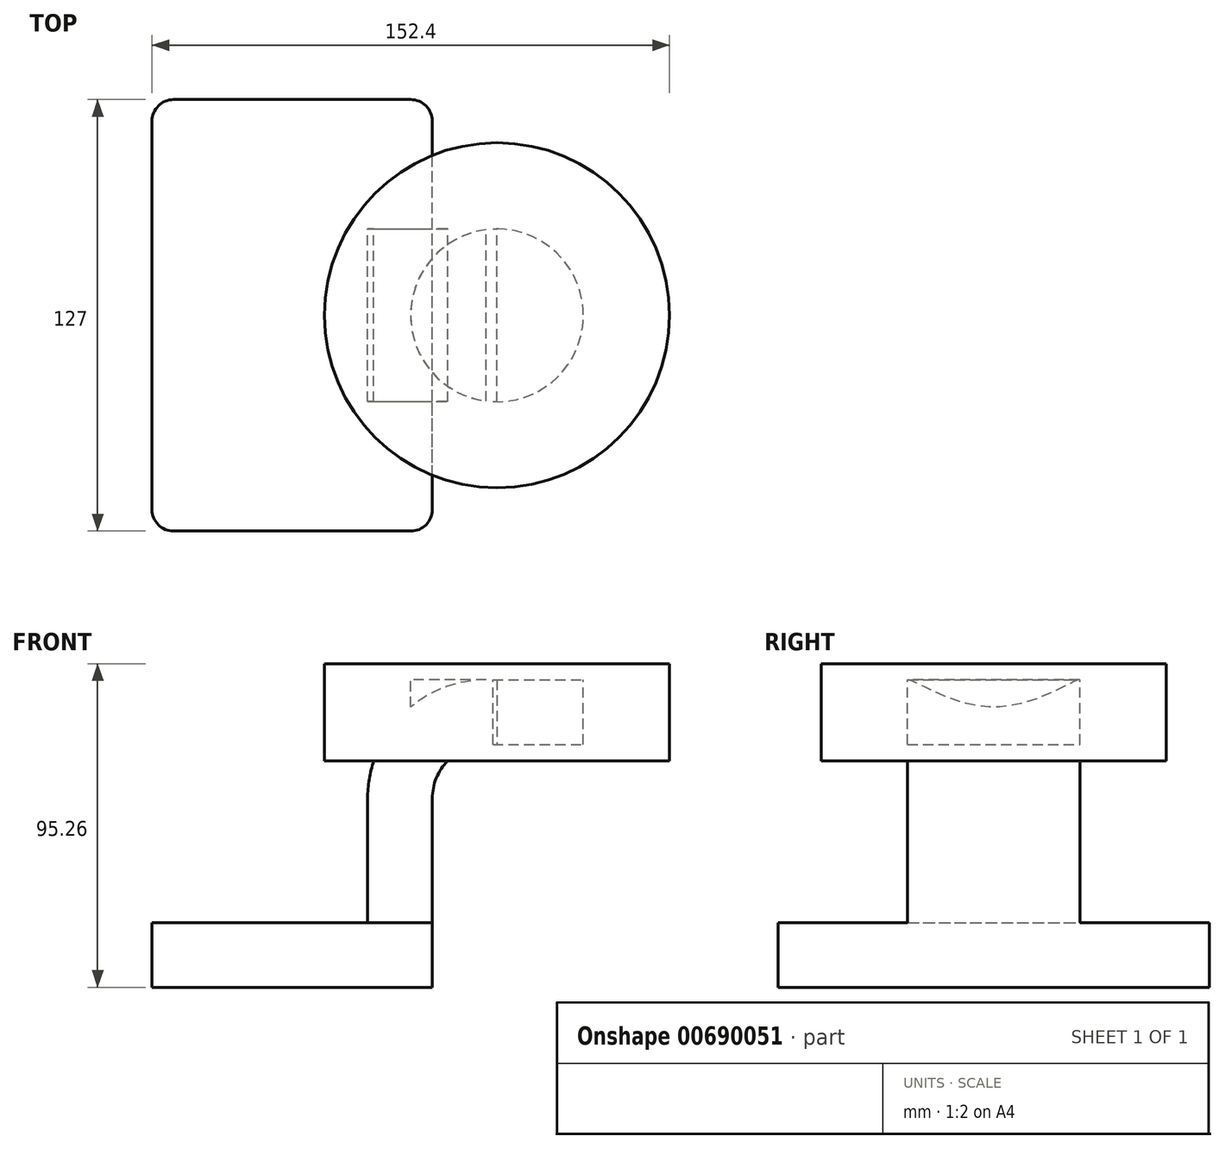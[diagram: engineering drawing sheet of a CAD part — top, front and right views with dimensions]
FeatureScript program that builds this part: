
annotation { "Feature Type Name" : "Feature", "Feature Type Description" : "" }
export const myFeature = defineFeature(function(context is Context, id is Id, definition is map)
    precondition{}
    {
        {
            var Q0;
            Q0=qCreatedBy(makeId("Front.planeOp"),FACE);
            var sketch = newSketch(context, id + "F0", { "sketchPlane" : qUnion([Q0])});
            skLineSegment(sketch, "E0.bottom", {"start": v(-41.28, -9.52) * mm, "end": v(41.28, -9.52) * mm});
            skLineSegment(sketch, "E0.top", {"start": v(-41.28, 9.53) * mm, "end": v(41.27, 9.53) * mm});
            skLineSegment(sketch, "E0.left", {"start": v(-41.27, -9.52) * mm, "end": v(-41.28, 9.53) * mm});
            skLineSegment(sketch, "E0.right", {"start": v(41.28, -9.52) * mm, "end": v(41.27, 9.53) * mm});
            skPoint(sketch, "E0.middle", {"position": v(0, 0) * mm});
            skLineSegment(sketch, "E1.bottom", {"start": v(111.12, 85.73) * mm, "end": v(60.32, 85.73) * mm});
            skLineSegment(sketch, "E1.top", {"start": v(111.12, 57.15) * mm, "end": v(60.32, 57.15) * mm});
            skLineSegment(sketch, "E1.left", {"start": v(111.12, 85.73) * mm, "end": v(111.12, 57.15) * mm});
            skLineSegment(sketch, "E1.right", {"start": v(60.32, 85.73) * mm, "end": v(60.32, 57.15) * mm});
            skPoint(sketch, "E1.middle", {"position": v(85.72, 71.44) * mm});
            skLineSegment(sketch, "E2", {"start": v(41.27, 9.53) * mm, "end": v(41.27, 46.05) * mm});
            skArc(sketch, "E3", {"start": v(41.27, 46.05) * mm, "mid": v(45.92, 57.28) * mm, "end": v(57.15, 61.93) * mm});
            skLineSegment(sketch, "E4", {"start": v(57.15, 61.93) * mm, "end": v(85.75, 61.93) * mm});
            skLineSegment(sketch, "E5.0", {"start": v(57.15, 80.98) * mm, "end": v(85.75, 80.98) * mm});
            skArc(sketch, "E5.1", {"start": v(22.22, 46.05) * mm, "mid": v(32.45, 70.75) * mm, "end": v(57.15, 80.98) * mm});
            skLineSegment(sketch, "E5.2", {"start": v(22.22, 9.53) * mm, "end": v(22.22, 46.05) * mm});
            skLineSegment(sketch, "E6", {"start": v(85.75, 61.93) * mm, "end": v(85.75, 80.98) * mm});
            skFitSpline(sketch, "E7", {"points": [v(-41.28, 9.53) * mm, v(57.15, 80.98) * mm], "startDerivative": vector(3.2, 106.89) * mm, "endDerivative": vector(105.52, -2.06) * mm});
            skSolve(sketch);
        }
        {
            var Q0;
            Q0=makeQuery(id+"F0.imprint","IMPRINT",FACE,{"disambiguationData":[TD([[makeQuery(id+"F0.imprint","IMPRINT",EDGE,{"derivedFrom":sQuery(id+"F0.wireOp",EDGE,"E0.bottom")}),1.0]])]});
            extrude(context, id + "F1", {"entities" : qUnion([Q0]), "endBound" : BoundingType.SYMMETRIC, "depth" : 127 * mm, "offsetDistance" : 25.4 * mm});
        }
        {
            var Q0;
            Q0=makeQuery(id+"F0.imprint","IMPRINT",FACE,{"disambiguationData":[TD([[makeQuery(id+"F0.imprint","IMPRINT",EDGE,{"derivedFrom":sQuery(id+"F0.wireOp",EDGE,"E5.1")}),1.0]])]});
            extrude(context, id + "F2", {"entities" : qUnion([Q0]), "operationType" : NewBodyOperationType.ADD, "endBound" : BoundingType.SYMMETRIC, "depth" : 15.88 * mm, "offsetDistance" : 25.4 * mm});
        }
        {
            var Q0;
            {var subQ0=sQuery(id+"F0.wireOp",EDGE,"E2");Q0=makeQuery(id+"F0.imprint","IMPRINT",FACE,{"disambiguationData":[TD([[makeQuery(id+"F0.imprint","IMPRINT",EDGE,{"derivedFrom":subQ0}),1.0]])]});}
            extrude(context, id + "F3", {"entities" : qUnion([Q0]), "operationType" : NewBodyOperationType.ADD, "endBound" : BoundingType.SYMMETRIC, "depth" : 50.8 * mm, "offsetDistance" : 25.4 * mm});
        }
        {
            var Q0;
            {var subQ1=sQuery(id+"F0.wireOp",EDGE,"E1.bottom");Q0=makeQuery(id+"F0.imprint","IMPRINT",FACE,{"disambiguationData":[TD([[makeQuery(id+"F0.imprint","IMPRINT",EDGE,{"derivedFrom":subQ1}),1.0]])]});}
            var Q1;
            Q1=sQuery(id+"F0.wireOp",EDGE,"E1.right");
            revolve(context, id + "F4", {"operationType" : NewBodyOperationType.ADD, "entities" : qUnion([Q0]), "axis" : qUnion([Q1]), "revolveType" : RevolveType.FULL});
        }
        {
            var Q0;
            Q0=makeQuery(id+"F1.opExtrude","CAP_EDGE",EDGE,{"disambiguationData":[OSD([sQuery(id+"F0.wireOp",EDGE,"E0.right")])],"isStart":false});
            var Q1;
            Q1=makeQuery(id+"F1.opExtrude","CAP_EDGE",EDGE,{"disambiguationData":[OSD([sQuery(id+"F0.wireOp",EDGE,"E0.left")])],"isStart":false});
            var Q2;
            Q2=makeQuery(id+"F1.opExtrude","CAP_EDGE",EDGE,{"disambiguationData":[OSD([sQuery(id+"F0.wireOp",EDGE,"E0.right")])],"isStart":true});
            var Q3;
            Q3=makeQuery(id+"F1.opExtrude","CAP_EDGE",EDGE,{"disambiguationData":[OSD([sQuery(id+"F0.wireOp",EDGE,"E0.left")])],"isStart":true});
            fillet(context, id + "F5", {"entities" : qUnion([Q0, Q1, Q2, Q3]), "radius" : 6.35 * mm, "tangentPropagation" : true, "allowEdgeOverflow" : false});
        }
    });
